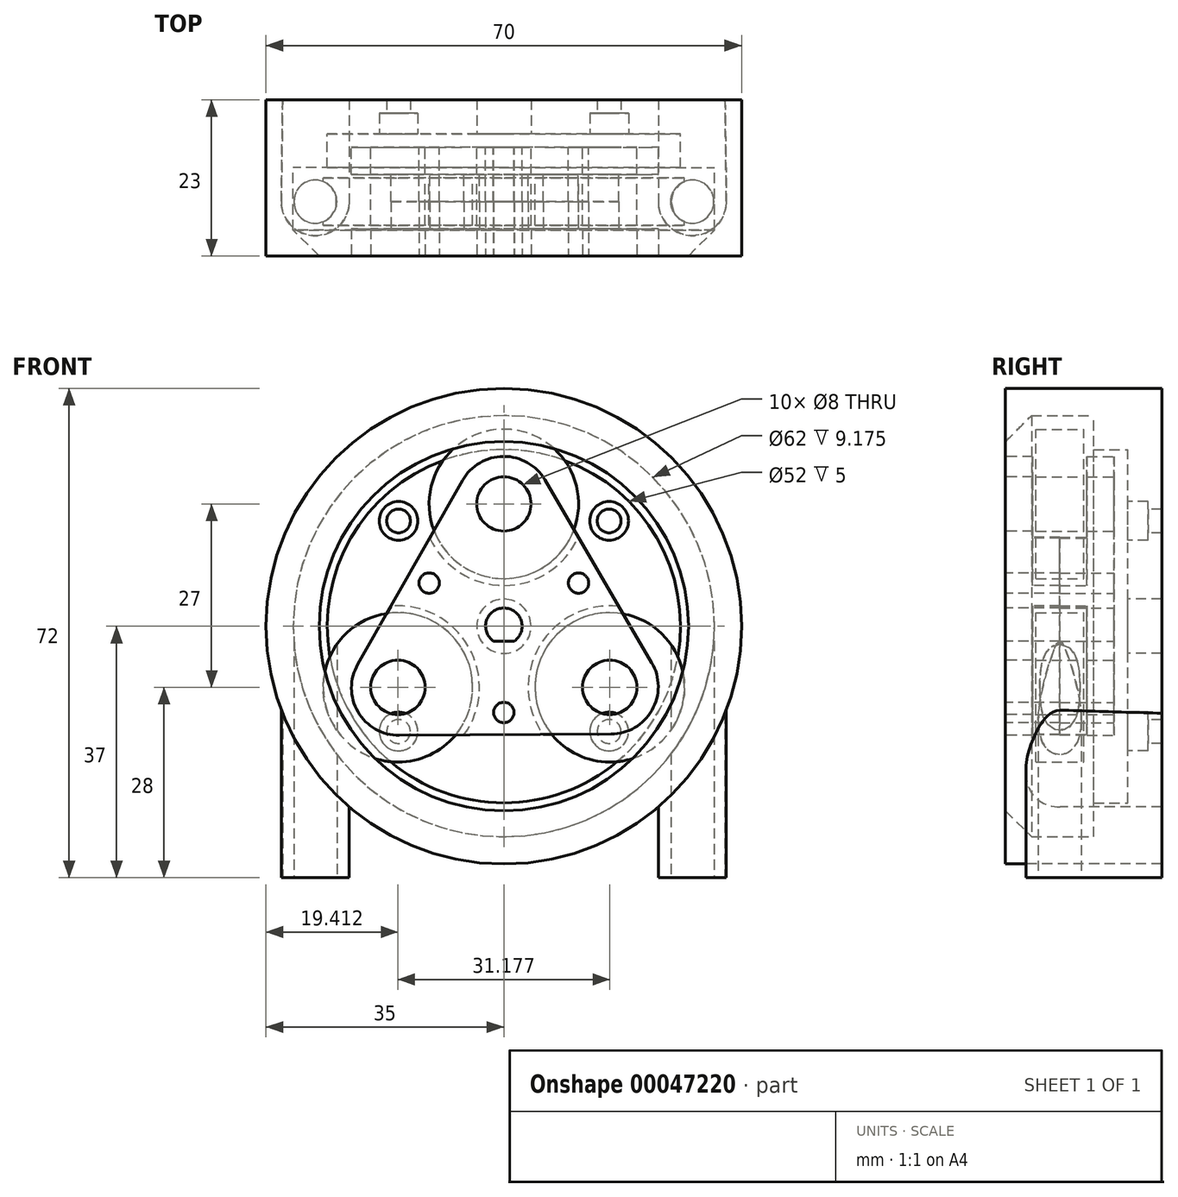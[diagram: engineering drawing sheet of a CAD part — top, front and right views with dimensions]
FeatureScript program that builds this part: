
annotation { "Feature Type Name" : "Feature", "Feature Type Description" : "" }
export const myFeature = defineFeature(function(context is Context, id is Id, definition is map)
    precondition{}
    {
        {
            var Q0;
            Q0=qCreatedBy(makeId("Front.planeOp"),FACE);
            var sketch = newSketch(context, id + "F0", { "sketchPlane" : qUnion([Q0])});
            skCircle(sketch, "E0", {"center": v(0, 18) * mm, "radius": 11 * mm, "construction": true});
            skLineSegment(sketch, "E1", {"start": v(0, 0) * mm, "end": v(0, 18) * mm, "construction": true});
            skCircle(sketch, "E2.1.0", {"center": v(-15.59, -9) * mm, "radius": 11 * mm, "construction": true});
            skLineSegment(sketch, "E2.1.1", {"start": v(0, 0) * mm, "end": v(-15.59, -9) * mm, "construction": true});
            skCircle(sketch, "E2.2.0", {"center": v(15.59, -9) * mm, "radius": 11 * mm, "construction": true});
            skLineSegment(sketch, "E2.2.1", {"start": v(0, 0) * mm, "end": v(15.59, -9) * mm, "construction": true});
            skPoint(sketch, "E2.center", {"position": v(0, 0) * mm});
            skArc(sketch, "E3", {"start": v(6.04, 21.53) * mm, "mid": v(-0.04, 25) * mm, "end": v(-6.08, 21.47) * mm});
            skArc(sketch, "E4.1.0", {"start": v(-21.5, -5.6) * mm, "mid": v(-21.47, -12.6) * mm, "end": v(-15.38, -16.07) * mm});
            skArc(sketch, "E4.2.0", {"start": v(15.77, -15.89) * mm, "mid": v(21.8, -12.36) * mm, "end": v(21.77, -5.36) * mm});
            skPoint(sketch, "E4.center", {"position": v(0.1, 0.01) * mm});
            skLineSegment(sketch, "E5", {"start": v(-21.5, -5.6) * mm, "end": v(-6.08, 21.47) * mm});
            skLineSegment(sketch, "E6.1.0", {"start": v(15.77, -15.89) * mm, "end": v(-15.38, -16.07) * mm});
            skLineSegment(sketch, "E6.2.0", {"start": v(6.04, 21.53) * mm, "end": v(21.77, -5.36) * mm});
            skCircle(sketch, "E7", {"center": v(0.1, 0.01) * mm, "radius": 32.82 * mm, "construction": true});
            skCircle(sketch, "E8", {"center": v(-15.59, -9) * mm, "radius": 4 * mm});
            skCircle(sketch, "E9.1.0", {"center": v(15.59, -9) * mm, "radius": 4 * mm});
            skCircle(sketch, "E9.2.0", {"center": v(0, 18) * mm, "radius": 4 * mm});
            skSolve(sketch);
        }
        {
            var Q0;
            Q0 = qSketchRegion(id + "F0", true);
            extrude(context, id + "F1", {"entities" : qUnion([Q0]), "depth" : 4 * mm});
        }
        {
            var Q0;
            Q0=makeQuery(id+"F1.opExtrude","CAP_FACE",FACE,{"disambiguationData":[OSD([sQuery(id+"F0.wireOp",EDGE,"E3"),sQuery(id+"F0.wireOp",EDGE,"E4.1.0"),sQuery(id+"F0.wireOp",EDGE,"E4.2.0"),sQuery(id+"F0.wireOp",EDGE,"E5"),sQuery(id+"F0.wireOp",EDGE,"E6.1.0"),sQuery(id+"F0.wireOp",EDGE,"E6.2.0"),sQuery(id+"F0.wireOp",EDGE,"E8"),sQuery(id+"F0.wireOp",EDGE,"E9.1.0"),sQuery(id+"F0.wireOp",EDGE,"E9.2.0")])],"isStart":false});
            var sketch = newSketch(context, id + "F2", { "sketchPlane" : qUnion([Q0])});
            skArc(sketch, "E10", {"start": v(-5.85, -16.01) * mm, "mid": v(-5.16, -3.07) * mm, "end": v(-16.63, 2.95) * mm});
            skArc(sketch, "E11", {"start": v(1.54, -2.19) * mm, "mid": v(0, 2.68) * mm, "end": v(-1.54, -2.19) * mm});
            skLineSegment(sketch, "E12", {"start": v(-1.54, -2.19) * mm, "end": v(1.54, -2.19) * mm});
            skArc(sketch, "E13.1.0", {"start": v(16.93, 2.93) * mm, "mid": v(5.25, -2.9) * mm, "end": v(5.8, -15.95) * mm});
            skArc(sketch, "E13.2.0", {"start": v(-10.9, 13) * mm, "mid": v(0.07, 6) * mm, "end": v(10.96, 13.12) * mm});
            skLineSegment(sketch, "E14.0", {"start": v(-16.63, 2.95) * mm, "end": v(-10.9, 13) * mm});
            skLineSegment(sketch, "E15.0", {"start": v(5.8, -15.95) * mm, "end": v(-5.85, -16.01) * mm});
            skLineSegment(sketch, "E16.0", {"start": v(10.96, 13.12) * mm, "end": v(16.93, 2.93) * mm});
            skPoint(sketch, "E17.orphan", {"position": v(-6.08, 21.47) * mm});
            skPoint(sketch, "E18.orphan", {"position": v(6.04, 21.53) * mm});
            skPoint(sketch, "E19.orphan", {"position": v(21.77, -5.36) * mm});
            skPoint(sketch, "E20.orphan", {"position": v(15.77, -15.89) * mm});
            skPoint(sketch, "E21.orphan", {"position": v(-15.38, -16.07) * mm});
            skPoint(sketch, "E22.orphan", {"position": v(-21.5, -5.6) * mm});
            skSolve(sketch);
        }
        {
            var Q0;
            Q0 = qSketchRegion(id + "F2", true);
            extrude(context, id + "F3", {"entities" : qUnion([Q0]), "operationType" : NewBodyOperationType.ADD, "depth" : 4 * mm});
        }
        {
            var Q0;
            Q0=qCreatedBy(makeId("Front.planeOp"),FACE);
            var sketch = newSketch(context, id + "F4", { "sketchPlane" : qUnion([Q0])});
            skLineSegment(sketch, "E23", {"start": v(0, 0) * mm, "end": v(0, -15.5) * mm, "construction": true});
            skCircle(sketch, "E24", {"center": v(0, -12.7) * mm, "radius": 1.5 * mm});
            skCircle(sketch, "E25.1.0", {"center": v(11, 6.35) * mm, "radius": 1.5 * mm});
            skCircle(sketch, "E25.2.0", {"center": v(-11, 6.35) * mm, "radius": 1.5 * mm});
            skPoint(sketch, "E25.center", {"position": v(0, 0) * mm});
            skArc(sketch, "E26.0", {"start": v(1.54, -2.19) * mm, "mid": v(0, 2.68) * mm, "end": v(-1.54, -2.19) * mm});
            skLineSegment(sketch, "E27.0", {"start": v(-1.54, -2.19) * mm, "end": v(1.54, -2.19) * mm});
            skSolve(sketch);
        }
        {
            var Q0;
            Q0 = qSketchRegion(id + "F4", true);
            extrude(context, id + "F5", {"entities" : qUnion([Q0]), "operationType" : NewBodyOperationType.REMOVE, "depth" : 25.4 * mm});
        }
        {
            var Q0;
            Q0=qCreatedBy(makeId("Front.planeOp"),FACE);
            cPlane(context, id + "F6", {"entities" : qUnion([Q0]), "cplaneType" : CPlaneType.OFFSET, "offset" : 2 * mm, "oppositeDirection" : true, "width" : 150 * mm, "height" : 150 * mm});
        }
        {
            var Q0;
            Q0=qCreatedBy(id+"F6.planeOp",FACE);
            var sketch = newSketch(context, id + "F7", { "sketchPlane" : qUnion([Q0])});
            skLineSegment(sketch, "E28", {"start": v(0, 0) * mm, "end": v(15.5, 15.5) * mm, "construction": true});
            skCircle(sketch, "E29", {"center": v(15.5, 15.5) * mm, "radius": 2.85 * mm});
            skCircle(sketch, "E30", {"center": v(0, 18) * mm, "radius": 11 * mm, "construction": true});
            skCircle(sketch, "E31", {"center": v(0, 0) * mm, "radius": 29 * mm, "construction": true});
            skCircle(sketch, "E32", {"center": v(0, 0) * mm, "radius": 35 * mm});
            skCircle(sketch, "E33.1.0", {"center": v(-15.5, 15.5) * mm, "radius": 2.85 * mm});
            skCircle(sketch, "E33.2.0", {"center": v(-15.5, -15.5) * mm, "radius": 2.85 * mm});
            skCircle(sketch, "E33.3.0", {"center": v(15.5, -15.5) * mm, "radius": 2.85 * mm});
            skCircle(sketch, "E34", {"center": v(0, 0) * mm, "radius": 4 * mm});
            skSolve(sketch);
        }
        {
            var Q0;
            Q0=makeQuery(id+"F7.imprint","IMPRINT",FACE,{"disambiguationData":[TD([[makeQuery(id+"F7.imprint","IMPRINT",EDGE,{"derivedFrom":sQuery(id+"F7.wireOp",EDGE,"E29")}),-1.0]])]});
            extrude(context, id + "F8", {"entities" : qUnion([Q0]), "operationType" : NewBodyOperationType.ADD, "oppositeDirection" : true, "depth" : 3 * mm});
        }
        {
            var Q0;
            Q0=makeQuery(id+"F8.opExtrude","CAP_FACE",FACE,{"disambiguationData":[OSD([sQuery(id+"F7.wireOp",EDGE,"E29"),sQuery(id+"F7.wireOp",EDGE,"E32"),sQuery(id+"F7.wireOp",EDGE,"E33.1.0"),sQuery(id+"F7.wireOp",EDGE,"E33.2.0"),sQuery(id+"F7.wireOp",EDGE,"E33.3.0"),sQuery(id+"F7.wireOp",EDGE,"E34")])],"isStart":false});
            var sketch = newSketch(context, id + "F9", { "sketchPlane" : qUnion([Q0])});
            skCircle(sketch, "E35.0", {"center": v(0, 0) * mm, "radius": 4 * mm});
            skLineSegment(sketch, "E36", {"start": v(0, 0) * mm, "end": v(15.5, 15.5) * mm, "construction": true});
            skCircle(sketch, "E37", {"center": v(15.5, 15.5) * mm, "radius": 1.75 * mm});
            skCircle(sketch, "E38.0", {"center": v(0, 0) * mm, "radius": 35 * mm});
            skCircle(sketch, "E39.1.0", {"center": v(-15.5, 15.5) * mm, "radius": 1.75 * mm});
            skCircle(sketch, "E39.2.0", {"center": v(-15.5, -15.5) * mm, "radius": 1.75 * mm});
            skCircle(sketch, "E39.3.0", {"center": v(15.5, -15.5) * mm, "radius": 1.75 * mm});
            skSolve(sketch);
        }
        {
            var Q0;
            Q0 = qSketchRegion(id + "F9", true);
            extrude(context, id + "F10", {"entities" : qUnion([Q0]), "operationType" : NewBodyOperationType.ADD, "depth" : 2 * mm});
        }
        {
            var Q0;
            {var subQ0=sQuery(id+"F0.wireOp",EDGE,"E4.1.0");var subQ1=sQuery(id+"F0.wireOp",EDGE,"E5");var subQ2=sQuery(id+"F0.wireOp",EDGE,"E6.1.0");var subQ3=sQuery(id+"F0.wireOp",EDGE,"E8");Q0=makeQuery(id+"F3.boolean.opBoolean","SPLIT",FACE,{"disambiguationData":[TD([makeQuery(id+"F1.opExtrude","SWEPT_FACE",FACE,{"disambiguationData":[OSD([subQ0])]})])],"derivedFrom":makeQuery(id+"F1.opExtrude","CAP_FACE",FACE,{"disambiguationData":[OSD([sQuery(id+"F0.wireOp",EDGE,"E3"),subQ0,sQuery(id+"F0.wireOp",EDGE,"E4.2.0"),subQ1,subQ2,sQuery(id+"F0.wireOp",EDGE,"E6.2.0"),subQ3,sQuery(id+"F0.wireOp",EDGE,"E9.1.0"),sQuery(id+"F0.wireOp",EDGE,"E9.2.0")])],"isStart":false})});}
            cPlane(context, id + "F11", {"entities" : qUnion([Q0]), "cplaneType" : CPlaneType.OFFSET, "offset" : .5 * mm, "width" : 150 * mm, "height" : 150 * mm});
        }
        {
            var Q0;
            Q0=qCreatedBy(id+"F11.planeOp",FACE);
            var sketch = newSketch(context, id + "F12", { "sketchPlane" : qUnion([Q0])});
            skCircle(sketch, "E40", {"center": v(0, 18) * mm, "radius": 11 * mm});
            skCircle(sketch, "E41.0", {"center": v(0, 18) * mm, "radius": 4 * mm});
            skCircle(sketch, "E42.1.0", {"center": v(-15.59, -9) * mm, "radius": 11 * mm});
            skCircle(sketch, "E42.1.1", {"center": v(-15.59, -9) * mm, "radius": 4 * mm});
            skCircle(sketch, "E42.2.0", {"center": v(15.59, -9) * mm, "radius": 11 * mm});
            skCircle(sketch, "E42.2.1", {"center": v(15.59, -9) * mm, "radius": 4 * mm});
            skPoint(sketch, "E42.center", {"position": v(0, 0) * mm});
            skSolve(sketch);
        }
        {
            var Q0;
            Q0 = qSketchRegion(id + "F12", true);
            extrude(context, id + "F13", {"entities" : qUnion([Q0]), "depth" : 7 * mm});
        }
        {
            var Q0;
            Q0=makeQuery(id+"F1.opExtrude","SWEPT_BODY",BODY,{"disambiguationData":[OSD([sQuery(id+"F0.wireOp",EDGE,"E3"),sQuery(id+"F0.wireOp",EDGE,"E4.1.0"),sQuery(id+"F0.wireOp",EDGE,"E4.2.0"),sQuery(id+"F0.wireOp",EDGE,"E5"),sQuery(id+"F0.wireOp",EDGE,"E6.1.0"),sQuery(id+"F0.wireOp",EDGE,"E6.2.0"),sQuery(id+"F0.wireOp",EDGE,"E8"),sQuery(id+"F0.wireOp",EDGE,"E9.1.0"),sQuery(id+"F0.wireOp",EDGE,"E9.2.0")])]});
            var Q1;
            Q1=makeQuery(id+"F3.opExtrude","CAP_FACE",FACE,{"disambiguationData":[OSD([sQuery(id+"F2.wireOp",EDGE,"E10"),sQuery(id+"F2.wireOp",EDGE,"E11"),sQuery(id+"F2.wireOp",EDGE,"E12"),sQuery(id+"F2.wireOp",EDGE,"E13.1.0"),sQuery(id+"F2.wireOp",EDGE,"E13.2.0"),sQuery(id+"F2.wireOp",EDGE,"E14.0"),sQuery(id+"F2.wireOp",EDGE,"E15.0"),sQuery(id+"F2.wireOp",EDGE,"E16.0")])],"isStart":false});
            mirror(context, id + "F14", {"operationType" : NewBodyOperationType.ADD, "entities" : qUnion([Q0]), "mirrorPlane" : qUnion([Q1])});
        }
        {
            var Q0;
            Q0=makeQuery(id+"F8.opExtrude","CAP_FACE",FACE,{"disambiguationData":[OSD([sQuery(id+"F7.wireOp",EDGE,"E29"),sQuery(id+"F7.wireOp",EDGE,"E32"),sQuery(id+"F7.wireOp",EDGE,"E33.1.0"),sQuery(id+"F7.wireOp",EDGE,"E33.2.0"),sQuery(id+"F7.wireOp",EDGE,"E33.3.0"),sQuery(id+"F7.wireOp",EDGE,"E34")])],"isStart":true});
            var sketch = newSketch(context, id + "F15", { "sketchPlane" : qUnion([Q0])});
            skCircle(sketch, "E43.0", {"center": v(0, 0) * mm, "radius": 35 * mm});
            skCircle(sketch, "E44", {"center": v(0, 0) * mm, "radius": 31 * mm});
            skSolve(sketch);
        }
        {
            var Q0;
            Q0=makeQuery(id+"F15.imprint","IMPRINT",FACE,{"disambiguationData":[TD([[makeQuery(id+"F15.imprint","IMPRINT",EDGE,{"derivedFrom":sQuery(id+"F15.wireOp",EDGE,"E43.0")}),1.0]])]});
            extrude(context, id + "F16", {"entities" : qUnion([Q0]), "operationType" : NewBodyOperationType.ADD, "depth" : 18 * mm});
        }
        {
            var Q0;
            Q0=qCreatedBy(makeId("Right.planeOp"),FACE);
            var sketch = newSketch(context, id + "F17", { "sketchPlane" : qUnion([Q0])});
            skLineSegment(sketch, "E45", {"start": v(-11, -32.17) * mm, "end": v(-16, -27.17) * mm});
            skLineSegment(sketch, "E46", {"start": v(-16, -27.17) * mm, "end": v(-16, -32.17) * mm});
            skLineSegment(sketch, "E47", {"start": v(-16, -32.17) * mm, "end": v(-11, -32.17) * mm});
            skLineSegment(sketch, "E48", {"start": v(0, 0) * mm, "end": v(-16.04, 0) * mm, "construction": true});
            skSolve(sketch);
        }
        {
            var Q0;
            Q0=makeQuery(id+"F17.imprint","IMPRINT",FACE,{"disambiguationData":[TD([[makeQuery(id+"F17.imprint","IMPRINT",EDGE,{"derivedFrom":sQuery(id+"F17.wireOp",EDGE,"E45")}),1.0]])]});
            var Q1;
            Q1=sQuery(id+"F17.wireOp",EDGE,"E48");
            revolve(context, id + "F18", {"operationType" : NewBodyOperationType.ADD, "entities" : qUnion([Q0]), "axis" : qUnion([Q1]), "revolveType" : RevolveType.FULL});
        }
        {
            var Q0;
            Q0=qCreatedBy(makeId("Top.planeOp"),FACE);
            cPlane(context, id + "F19", {"entities" : qUnion([Q0]), "cplaneType" : CPlaneType.OFFSET, "offset" : 37 * mm, "oppositeDirection" : true, "width" : 150 * mm, "height" : 150 * mm});
        }
        {
            var Q0;
            Q0=qCreatedBy(id+"F19.planeOp",FACE);
            var sketch = newSketch(context, id + "F20", { "sketchPlane" : qUnion([Q0])});
            skArc(sketch, "E49", {"start": v(-32.75, -7.94) * mm, "mid": v(-27.76, -13) * mm, "end": v(-22.75, -7.96) * mm});
            skLineSegment(sketch, "E50", {"start": v(-22.75, -7.96) * mm, "end": v(-22.75, 7) * mm});
            skLineSegment(sketch, "E51", {"start": v(-22.75, 7) * mm, "end": v(-32.57, 7) * mm});
            skLineSegment(sketch, "E52", {"start": v(-32.57, 7) * mm, "end": v(-32.75, -7.94) * mm});
            skLineSegment(sketch, "E53", {"start": v(0, 0) * mm, "end": v(0, -40.15) * mm, "construction": true});
            skArc(sketch, "E54.MirrorCS", {"start": v(32.75, -7.94) * mm, "mid": v(27.76, -13) * mm, "end": v(22.75, -7.96) * mm});
            skLineSegment(sketch, "E55.MirrorCS", {"start": v(32.57, 7) * mm, "end": v(32.75, -7.94) * mm});
            skLineSegment(sketch, "E56.MirrorCS", {"start": v(22.75, -7.96) * mm, "end": v(22.75, 7) * mm});
            skLineSegment(sketch, "E57.MirrorCS", {"start": v(22.75, 7) * mm, "end": v(32.57, 7) * mm});
            skSolve(sketch);
        }
        {
            var Q0;
            Q0 = qSketchRegion(id + "F20", true);
            var Q1;
            Q1=makeQuery(id+"F16.boolean.opBoolean","MERGE",FACE,{"derivedFrom":[makeQuery(id+"F10.boolean.opBoolean","MERGE",FACE,{"derivedFrom":[makeQuery(id+"F8.opExtrude","SWEPT_FACE",FACE,{"disambiguationData":[OSD([sQuery(id+"F7.wireOp",EDGE,"E32")])]}),makeQuery(id+"F10.opExtrude","SWEPT_FACE",FACE,{"disambiguationData":[OSD([sQuery(id+"F9.wireOp",EDGE,"E38.0")])]})]}),makeQuery(id+"F16.opExtrude","SWEPT_FACE",FACE,{"disambiguationData":[OSD([sQuery(id+"F15.wireOp",EDGE,"E43.0")])]})]});
            extrude(context, id + "F21", {"entities" : qUnion([Q0]), "operationType" : NewBodyOperationType.ADD, "endBound" : BoundingType.UP_TO_SURFACE, "endBoundEntityFace" : qUnion([Q1]), "depth" : 25 * mm});
        }
        {
            var Q0;
            Q0=makeQuery(id+"F21.opExtrude","CAP_FACE",FACE,{"disambiguationData":[OSD([sQuery(id+"F20.wireOp",EDGE,"E54.MirrorCS"),sQuery(id+"F20.wireOp",EDGE,"E55.MirrorCS"),sQuery(id+"F20.wireOp",EDGE,"E56.MirrorCS"),sQuery(id+"F20.wireOp",EDGE,"E57.MirrorCS")])],"isStart":true});
            var sketch = newSketch(context, id + "F22", { "sketchPlane" : qUnion([Q0])});
            skCircle(sketch, "E58.0", {"center": v(27.75, 8) * mm, "radius": 3.17 * mm});
            skCircle(sketch, "E59.0", {"center": v(-27.75, 8) * mm, "radius": 3.17 * mm});
            skSolve(sketch);
        }
        {
            var Q0;
            Q0 = qSketchRegion(id + "F22", true);
            var Q1;
            Q1=makeQuery(id+"F16.opExtrude","SWEPT_FACE",FACE,{"disambiguationData":[OSD([sQuery(id+"F15.wireOp",EDGE,"E44")])]});
            extrude(context, id + "F23", {"entities" : qUnion([Q0]), "operationType" : NewBodyOperationType.REMOVE, "oppositeDirection" : true, "endBoundEntityFace" : qUnion([Q1]), "depth" : 37 * mm});
        }
        {
            var Q0;
            Q0=makeQuery(id+"F8.opExtrude","CAP_FACE",FACE,{"disambiguationData":[OSD([sQuery(id+"F7.wireOp",EDGE,"E29"),sQuery(id+"F7.wireOp",EDGE,"E32"),sQuery(id+"F7.wireOp",EDGE,"E33.1.0"),sQuery(id+"F7.wireOp",EDGE,"E33.2.0"),sQuery(id+"F7.wireOp",EDGE,"E33.3.0"),sQuery(id+"F7.wireOp",EDGE,"E34")])],"isStart":true});
            var sketch = newSketch(context, id + "F24", { "sketchPlane" : qUnion([Q0])});
            skCircle(sketch, "E60", {"center": v(0, 0) * mm, "radius": 26 * mm});
            skCircle(sketch, "E61.0", {"center": v(0, 0) * mm, "radius": 31 * mm});
            skSolve(sketch);
        }
        {
            var Q0;
            Q0=makeQuery(id+"F24.imprint","IMPRINT",FACE,{"disambiguationData":[TD([[makeQuery(id+"F24.imprint","IMPRINT",EDGE,{"derivedFrom":sQuery(id+"F24.wireOp",EDGE,"E60")}),-1.0]])]});
            extrude(context, id + "F25", {"entities" : qUnion([Q0]), "operationType" : NewBodyOperationType.ADD, "depth" : 5 * mm});
        }
    });
